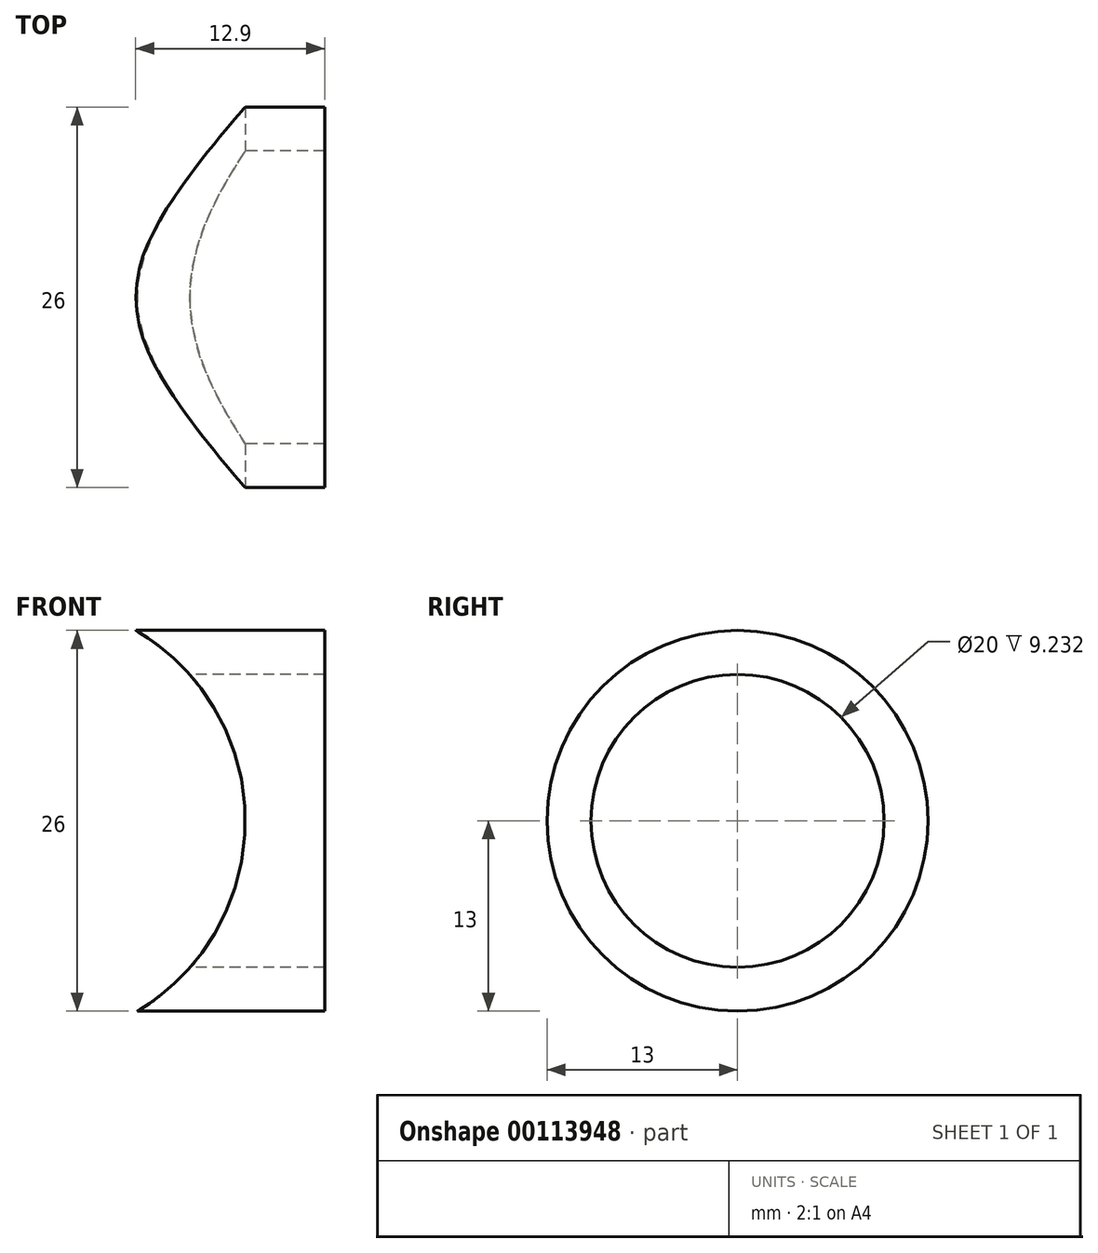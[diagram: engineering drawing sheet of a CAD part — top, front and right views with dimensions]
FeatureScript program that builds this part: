
annotation { "Feature Type Name" : "Feature", "Feature Type Description" : "" }
export const myFeature = defineFeature(function(context is Context, id is Id, definition is map)
    precondition{}
    {
        {
            var Q0;
            Q0=qCreatedBy(makeId("Right.planeOp"),FACE);
            var sketch = newSketch(context, id + "F0", { "sketchPlane" : qUnion([Q0])});
            skCircle(sketch, "E0", {"center": v(0, 0) * mm, "radius": 10 * mm});
            skCircle(sketch, "E1.0", {"center": v(0, 0) * mm, "radius": 13 * mm});
            skSolve(sketch);
        }
        {
            var Q0;
            Q0=makeQuery(id+"F0.imprint","IMPRINT",FACE,{"disambiguationData":[TD([[makeQuery(id+"F0.imprint","IMPRINT",EDGE,{"derivedFrom":sQuery(id+"F0.wireOp",EDGE,"E0")}),-1.0]])]});
            extrude(context, id + "F1", {"entities" : qUnion([Q0]), "depth" : 44.16 * mm, "hasSecondDirection" : true, "secondDirectionOppositeDirection" : false, "secondDirectionDepth" : 30.94 * mm});
        }
        {
            var Q0;
            Q0=qCreatedBy(makeId("Front.planeOp"),FACE);
            var sketch = newSketch(context, id + "F2", { "sketchPlane" : qUnion([Q0])});
            skLineSegment(sketch, "E2.bottom", {"start": v(25.47, -15) * mm, "end": v(-32.5, -15) * mm});
            skLineSegment(sketch, "E2.top", {"start": v(24.94, 15) * mm, "end": v(-32.5, 15) * mm});
            skLineSegment(sketch, "E2.right", {"start": v(-32.5, -15) * mm, "end": v(-32.5, 15) * mm});
            skPoint(sketch, "E2.middle", {"position": v(0, 0) * mm});
            skArc(sketch, "E3", {"start": v(25.47, -15) * mm, "mid": v(38.67, 1.51) * mm, "end": v(22.4, 15) * mm});
            skPoint(sketch, "E4.orphan", {"position": v(32.5, 15) * mm});
            skPoint(sketch, "E5.orphan", {"position": v(32.5, -15) * mm});
            skArc(sketch, "E6.0", {"start": v(25, -11.03) * mm, "mid": v(25.2, -11) * mm, "end": v(25.4, -10.97) * mm});
            skSolve(sketch);
        }
        {
            var Q0;
            {var subQ5=sQuery(id+"F2.wireOp",EDGE,"E2.bottom");Q0=makeQuery(id+"F2.imprint","IMPRINT",FACE,{"disambiguationData":[TD([[makeQuery(id+"F2.imprint","IMPRINT",EDGE,{"derivedFrom":subQ5}),-1.0]])]});}
            extrude(context, id + "F3", {"entities" : qUnion([Q0]), "operationType" : NewBodyOperationType.REMOVE, "endBound" : BoundingType.SYMMETRIC, "oppositeDirection" : true, "depth" : 130.2 * mm});
        }
    });
